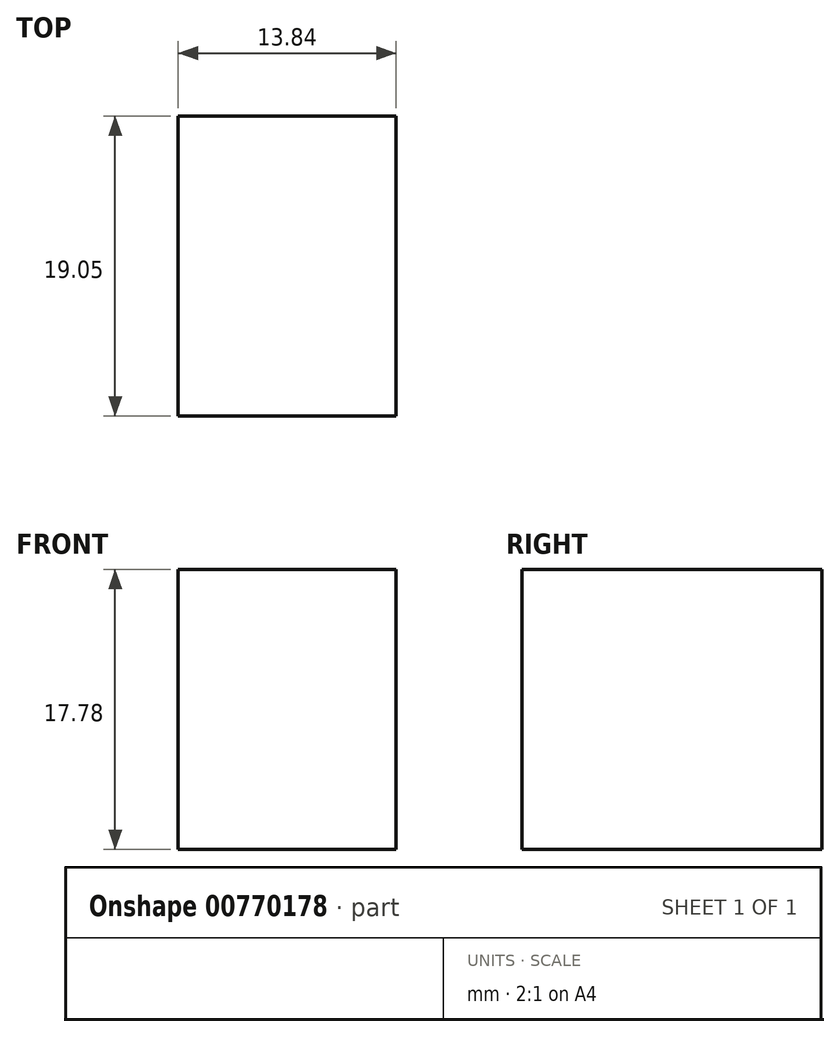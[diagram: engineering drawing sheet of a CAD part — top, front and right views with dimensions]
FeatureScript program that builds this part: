
annotation { "Feature Type Name" : "Feature", "Feature Type Description" : "" }
export const myFeature = defineFeature(function(context is Context, id is Id, definition is map)
    precondition{}
    {
        {
            var Q0;
            Q0=qCreatedBy(makeId("Right.planeOp"),FACE);
            var sketch = newSketch(context, id + "F0", { "sketchPlane" : qUnion([Q0])});
            skLineSegment(sketch, "E0.bottom", {"start": v(-19.05, 18.43) * mm, "end": v(0, 18.43) * mm});
            skLineSegment(sketch, "E0.top", {"start": v(-19.05, 36.21) * mm, "end": v(0, 36.21) * mm});
            skLineSegment(sketch, "E0.left", {"start": v(-19.05, 18.43) * mm, "end": v(-19.05, 36.21) * mm});
            skLineSegment(sketch, "E0.right", {"start": v(0, 18.43) * mm, "end": v(0, 36.21) * mm});
            skSolve(sketch);
        }
        {
            var Q0;
            Q0=makeQuery(id+"F0.imprint","IMPRINT",FACE,{"disambiguationData":[TD([[makeQuery(id+"F0.imprint","IMPRINT",EDGE,{"derivedFrom":sQuery(id+"F0.wireOp",EDGE,"E0.bottom")}),1.0]])]});
            extrude(context, id + "F1", {"entities" : qUnion([Q0]), "depth" : 13.84 * mm, "offsetDistance" : 25.4 * mm});
        }
    });
